# Revit family: Ebara-Grupo de presión-AP MATRIX VV (350-ES-600)
name_source: partatom
category: Equipos mecánicos
revit_build: Autodesk Revit 2017 (Build: 20171027_0315(x64)
units: mm (PartAtom-declared; Revit-internal decimal feet)

## family parameters
Compartido = No
Corte con vacíos al cargar = No
Cota de conector redondo = Diámetro de uso
Número OmniClass = 23.65.05.11.11
Punto de cálculo de habitación = No
Se basa en plano de trabajo = No
Siempre vertical = Sí
Tipo de pieza = Normal
Título OmniClass = Water Supply Systems

## types (1)
- Ebara-Grupo de presión-AP MATRIX VV (350-ES-600)
    Acabado coloreado = 09 96_Genérico_Esmalte azul 30.137.225
    Acabado estructura = 09 96_Genérico_Esmalte negro 22.22.22
    Acabado metal blanco = 09 96_Genérico_Esmalte blanco 255.255.255
    Acabado plásticos = 06 60_Genérico_Plástico gris mate 128.128.128
    Acabado tuberías = 05 12_Genérico_Acero inoxidable AISI 304
    B00 = Ebara-Grupo de presión-Sin bomba (350-ES-600) : Sin bomba
    B01 = Ebara-Grupo de presión-Bomba MATRIX (350-ES-600) : 5-4
    B02 = Ebara-Grupo de presión-Bomba MATRIX (350-ES-600) : 5-5
    B03 = Ebara-Grupo de presión-Bomba MATRIX (350-ES-600) : 5-6
    B04 = Ebara-Grupo de presión-Bomba MATRIX (350-ES-600) : 5-7
    B05 = Ebara-Grupo de presión-Bomba MATRIX (350-ES-600) : 5-8
    B06 = Ebara-Grupo de presión-Bomba MATRIX (350-ES-600) : 5-9
    B07 = Ebara-Grupo de presión-Bomba MATRIX (350-ES-600) : 10-3
    B08 = Ebara-Grupo de presión-Bomba MATRIX (350-ES-600) : 10-4
    B09 = Ebara-Grupo de presión-Bomba MATRIX (350-ES-600) : 10-5
    B10 = Ebara-Grupo de presión-Bomba MATRIX (350-ES-600) : 10-6
    B11 = Ebara-Grupo de presión-Bomba MATRIX (350-ES-600) : 18-3
    B12 = Ebara-Grupo de presión-Bomba MATRIX (350-ES-600) : 18-4
    B13 = Ebara-Grupo de presión-Bomba MATRIX (350-ES-600) : 18-5
    B14 = Ebara-Grupo de presión-Bomba MATRIX (350-ES-600) : 18-6
    Bancada 1 = Ebara-Grupo de presión-Bancada (350-ES-600) : Series 5, 10 y 18-3
    Bancada 2 = Ebara-Grupo de presión-Bancada (350-ES-600) : Serie 18 - 4, 5 y 6
    Código de montaje = 50.10.10.20
    Fabricante = Ebara
    Modelo = AP MATRIX
    URL = http://www.ebara.es
